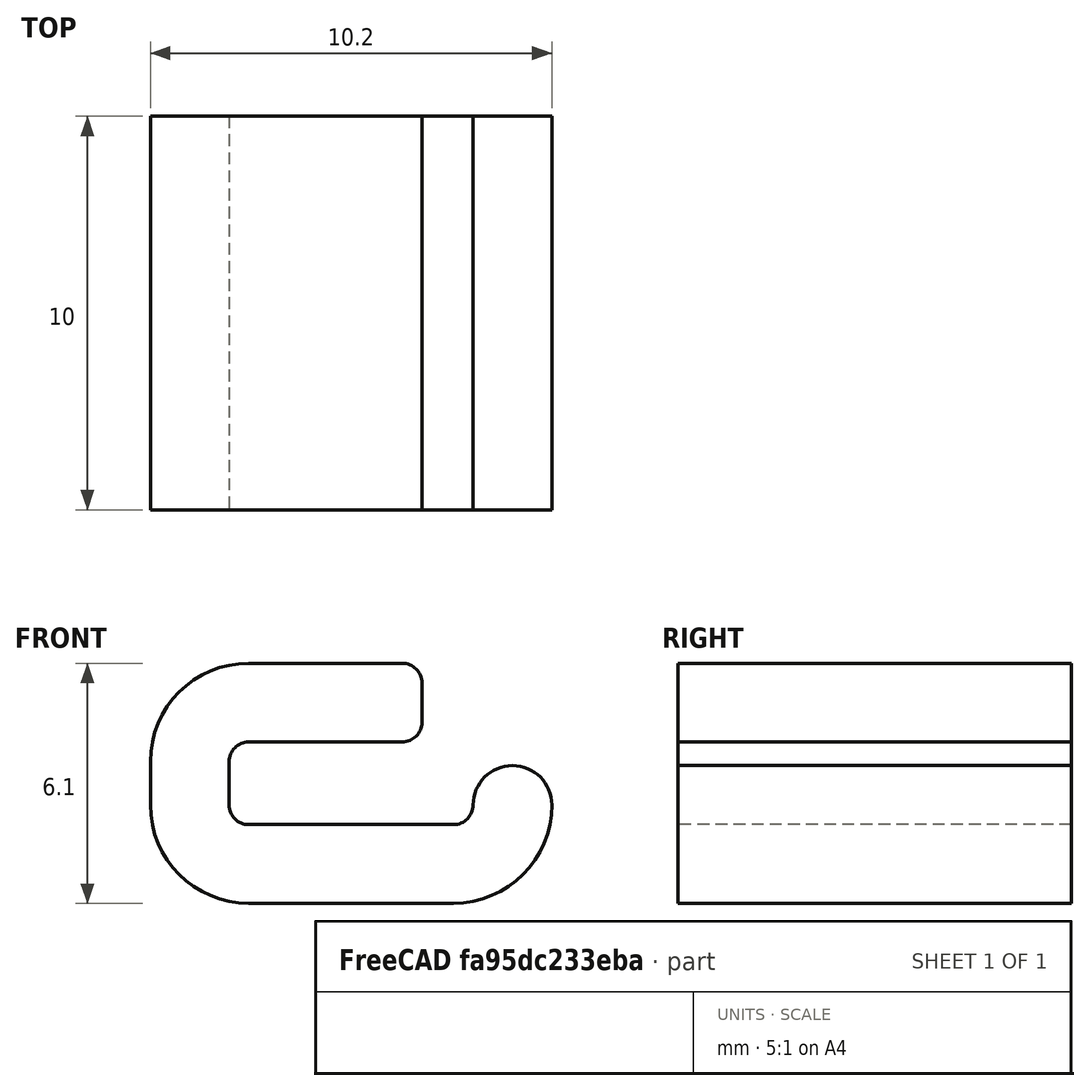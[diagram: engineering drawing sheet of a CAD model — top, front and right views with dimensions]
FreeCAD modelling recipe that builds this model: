
FCSTD DOCUMENT  (FreeCAD 1.1R20260414 (Git shallow))
Label: GT2 6mm Belt Clip
License: Creative Commons Attribution 4.0
LicenseURL: https://creativecommons.org/licenses/by/4.0/
objects: App::Point×1, Sketcher::SketchObject×1, PartDesign::Pad×1, PartDesign::Body×1
note: 6 computed .brp shape members not serialized (recipe doc carries the construction recipe); baked Part::Feature solids carry a one-line shape summary decoded from their .brp

FEATURE [App::Point] Origin001
  Role = Origin
FEATURE [Sketcher::SketchObject] Sketch
  ArcFitTolerance = 1e-06
  AttachmentSupport = -> [Origin]
  ExternalTypes = [0]
  FullyConstrained = true
  MakeInternals = true
  MapMode = 5
  Placement = pos=(0,0,0) rot=(1,0,0;1.5708rad)
  _ExternalGeoVersion = 1
  sketch-geometry (27):
    g0: LineSegment StartX=-2.45 StartY=0.55 StartZ=0 EndX=-2.45 EndY=-0.55 EndZ=0
    g1: LineSegment StartX=-1.95 StartY=-1.05 StartZ=0 EndX=1.95 EndY=-1.05 EndZ=0
    g2: LineSegment [constr] StartX=2.45 StartY=-0.55 StartZ=0 EndX=2.45 EndY=0.55 EndZ=0
    g3: LineSegment StartX=1.95 StartY=1.05 StartZ=0 EndX=-1.95 EndY=1.05 EndZ=0
    g4: ArcOfCircle CenterX=-1.95 CenterY=0.55 CenterZ=0 NormalX=0 NormalY=0 NormalZ=1 AngleXU=0 Radius=0.5 StartAngle=1.5708 EndAngle=3.14159
    g5: ArcOfCircle CenterX=-1.95 CenterY=-0.55 CenterZ=0 NormalX=0 NormalY=0 NormalZ=1 AngleXU=0 Radius=0.5 StartAngle=3.14159 EndAngle=4.71239
    g6: ArcOfCircle [constr] CenterX=1.95 CenterY=-0.55 CenterZ=0 NormalX=0 NormalY=0 NormalZ=1 AngleXU=0 Radius=0.5 StartAngle=4.71239 EndAngle=6.28319
    g7: ArcOfCircle [constr] CenterX=1.95 CenterY=0.55 CenterZ=0 NormalX=0 NormalY=0 NormalZ=1 AngleXU=0 Radius=0.5 StartAngle=0 EndAngle=1.5708
    g8: LineSegment StartX=-4.45 StartY=0.55 StartZ=0 EndX=-4.45 EndY=-0.55 EndZ=0
    g9: LineSegment StartX=-1.95 StartY=-3.05 StartZ=0 EndX=1.95 EndY=-3.05 EndZ=0
    g10: LineSegment [constr] StartX=4.45 StartY=-0.55 StartZ=0 EndX=4.45 EndY=0.55 EndZ=0
    g11: LineSegment StartX=1.95 StartY=3.05 StartZ=0 EndX=-1.95 EndY=3.05 EndZ=0
    g12: ArcOfCircle CenterX=-1.95 CenterY=0.55 CenterZ=0 NormalX=0 NormalY=0 NormalZ=1 AngleXU=0 Radius=2.5 StartAngle=1.5708 EndAngle=3.14159
    g13: ArcOfCircle CenterX=-1.95 CenterY=-0.55 CenterZ=0 NormalX=0 NormalY=0 NormalZ=1 AngleXU=0 Radius=2.5 StartAngle=3.14159 EndAngle=4.71239
    g14: ArcOfCircle [constr] CenterX=1.95 CenterY=-0.55 CenterZ=0 NormalX=0 NormalY=0 NormalZ=1 AngleXU=0 Radius=2.5 StartAngle=4.71239 EndAngle=6.28319
    g15: ArcOfCircle [constr] CenterX=1.95 CenterY=0.55 CenterZ=0 NormalX=0 NormalY=0 NormalZ=1 AngleXU=0 Radius=2.5 StartAngle=0 EndAngle=1.5708
    g16: GeomPoint [constr] X=2.45 Y=-1.05 Z=0
    g17: GeomPoint [constr] X=0 Y=0 Z=0
    g18: ArcOfCircle CenterX=1.95 CenterY=2.55 CenterZ=0 NormalX=0 NormalY=0 NormalZ=1 AngleXU=0 Radius=0.5 StartAngle=2e-16 EndAngle=1.5708
    g19: LineSegment StartX=2.45 StartY=2.55 StartZ=0 EndX=2.45 EndY=1.55 EndZ=0
    g20: LineSegment StartX=3.25 StartY=-1.05 StartZ=0 EndX=1.95 EndY=-1.05 EndZ=0
    g21: ArcOfCircle CenterX=3.25 CenterY=-0.55 CenterZ=0 NormalX=0 NormalY=0 NormalZ=1 AngleXU=0 Radius=0.5 StartAngle=4.71239 EndAngle=6.28319
    g22: LineSegment StartX=1.95 StartY=-3.05 StartZ=0 EndX=3.25 EndY=-3.05 EndZ=0
    g23: ArcOfCircle CenterX=3.25 CenterY=-0.55 CenterZ=0 NormalX=0 NormalY=0 NormalZ=1 AngleXU=0 Radius=2.5 StartAngle=4.71239 EndAngle=6.28319
    g24: ArcOfCircle CenterX=4.75 CenterY=-0.55 CenterZ=0 NormalX=0 NormalY=0 NormalZ=1 AngleXU=0 Radius=1 StartAngle=0 EndAngle=3.14159
    g25: ArcOfCircle CenterX=1.95 CenterY=1.55 CenterZ=0 NormalX=0 NormalY=0 NormalZ=1 AngleXU=0 Radius=0.5 StartAngle=4.71239 EndAngle=6.28319
    g26: LineSegment [constr] StartX=2.35 StartY=1.25 StartZ=0 EndX=3.95 EndY=0.05 EndZ=0
  constraints (60):
    c: Tangent(g0,g4) = -1.5708
    c: Tangent(g0,g5) = -1.5708
    c: Tangent(g1,g5) = -1.5708
    c: Tangent(g1,g6) = -1.5708
    c: Tangent(g2,g6) = -1.5708
    c: Tangent(g2,g7) = -1.5708
    c: Tangent(g3,g7) = -1.5708
    c: Tangent(g3,g4) = -1.5708
    c: Vertical(g0)
    c: Vertical(g2)
    c: Horizontal(g1)
    c: Horizontal(g3)
    c: Equal(g4,g5)
    c: Equal(g5,g6)
    c: Equal(g6,g7)
    c: Tangent(g8,g12) = -1.5708
    c: Tangent(g8,g13) = -1.5708
    c: Tangent(g9,g13) = -1.5708
    c: Tangent(g9,g14) = -1.5708
    c: Tangent(g10,g14) = -1.5708
    c: Tangent(g10,g15) = -1.5708
    c: Tangent(g11,g15) = -1.5708
    c: Tangent(g11,g12) = -1.5708
    c: Coincident(g4,g12)
    c: Coincident(g5,g13)
    c: Coincident(g6,g14)
    c: Coincident(g7,g15)
    c: Vertical(g8)
    c: Vertical(g10)
    c: Horizontal(g9)
    c: Symmetric(g2,g0,g17)
    c: PointOnObject(g16,g1)
    c: PointOnObject(g16,g2)
    c: Coincident(g17,g-1)
    c: Distance(g3,g11) = 2
    c: Distance(g1,g3) = 2.1
    c: Radius(g4) = 0.5
    c: Tangent(g11,g18) = -1.5708
    c: Tangent(g18,g19) = 1.5708
    c: Vertical(g19)
    c: Vertical(g19,g2)
    c: Coincident(g1,g20)
    c: Horizontal(g20)
    c: Tangent(g21,g20) = 1.5708
    c: Coincident(g9,g22)
    c: Horizontal(g22)
    c: Tangent(g22,g23) = -1.5708
    c: Coincident(g21,g23)
    c: Horizontal(g21,g23)
    c: Radius(g21) = 0.5
    c: Tangent(g24,g23) = -1.5708
    c: Tangent(g24,g21) = 1.5708
    c: Tangent(g25,g19) = 1.5708
    c: Tangent(g25,g3) = 1.5708
    c: PointOnObject(g26,g25)
    c: PointOnObject(g26,g24)
    c: Perpendicular(g25,g26)
    c: Perpendicular(g24,g26)
    c: Distance(g26,g26) = 2
    c: Distance(g21,g0) = 6.2
FEATURE [PartDesign::Pad] Pad
  Direction = (0,-1,0)
  Length = 10
  Length2 = 10
  Profile = -> Sketch
  ReferenceAxis = -> Sketch [N_Axis]
  Refine = true
  SideType = 0
  Suppressed = false
  Type = 0
  Type2 = 0
FEATURE [PartDesign::Body] Body
  AllowCompound = false
  Group = -> [Sketch,Pad]
  Origin = -> Origin
  Tip = -> Pad
